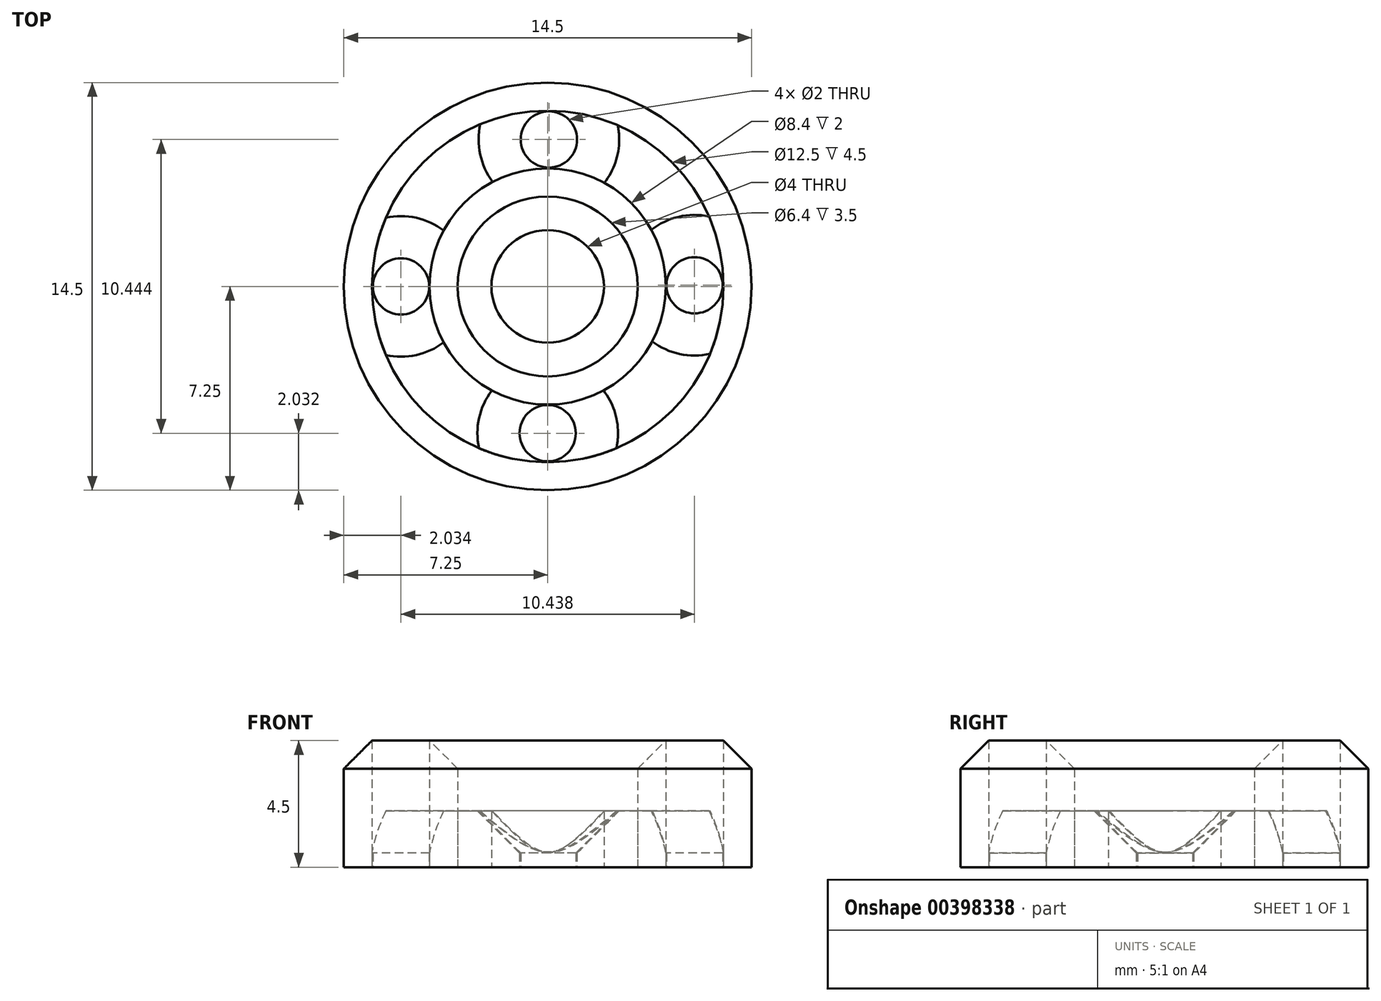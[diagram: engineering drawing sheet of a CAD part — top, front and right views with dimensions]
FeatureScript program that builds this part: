
annotation { "Feature Type Name" : "Feature", "Feature Type Description" : "" }
export const myFeature = defineFeature(function(context is Context, id is Id, definition is map)
    precondition{}
    {
        {
            var Q0;
            Q0=qCreatedBy(makeId("Top.planeOp"),FACE);
            var sketch = newSketch(context, id + "F0", { "sketchPlane" : qUnion([Q0])});
            skCircle(sketch, "E0", {"center": v(0, 0) * mm, "radius": 3.2 * mm});
            skCircle(sketch, "E1", {"center": v(0, 0) * mm, "radius": 4.2 * mm});
            skCircle(sketch, "E2", {"center": v(0, 0) * mm, "radius": 6.25 * mm});
            skCircle(sketch, "E3", {"center": v(0, 0) * mm, "radius": 7.25 * mm});
            skCircle(sketch, "E4", {"center": v(-5.22, 0) * mm, "radius": 1 * mm});
            skCircle(sketch, "E5", {"center": v(0, -5.22) * mm, "radius": 1 * mm});
            skCircle(sketch, "E6", {"center": v(0, 0) * mm, "radius": 2 * mm});
            skCircle(sketch, "E7", {"center": v(5.22, 0.04) * mm, "radius": 1 * mm});
            skCircle(sketch, "E8", {"center": v(0.04, 5.23) * mm, "radius": 1 * mm});
            skSolve(sketch);
        }
        {
            var Q0;
            Q0=makeQuery(id+"F0.imprint","IMPRINT",FACE,{"disambiguationData":[TD([[makeQuery(id+"F0.imprint","IMPRINT",EDGE,{"derivedFrom":sQuery(id+"F0.wireOp",EDGE,"E2")}),-1.0]])]});
            var Q1;
            Q1=makeQuery(id+"F0.imprint","IMPRINT",FACE,{"disambiguationData":[TD([[makeQuery(id+"F0.imprint","IMPRINT",EDGE,{"derivedFrom":sQuery(id+"F0.wireOp",EDGE,"E0")}),-1.0]])]});
            extrude(context, id + "F1", {"entities" : qUnion([Q0, Q1]), "depth" : 5 * mm});
        }
        {
            var Q0;
            Q0=makeQuery(id+"F0.imprint","IMPRINT",FACE,{"disambiguationData":[TD([[makeQuery(id+"F0.imprint","IMPRINT",EDGE,{"derivedFrom":sQuery(id+"F0.wireOp",EDGE,"E0")}),1.0]])]});
            var Q1;
            Q1=makeQuery(id+"F0.imprint","IMPRINT",FACE,{"disambiguationData":[TD([[makeQuery(id+"F0.imprint","IMPRINT",EDGE,{"derivedFrom":sQuery(id+"F0.wireOp",EDGE,"E2")}),1.0]])]});
            extrude(context, id + "F2", {"entities" : qUnion([Q0, Q1]), "depth" : 2 * mm});
        }
        {
            var Q0;
            Q0=makeQuery(id+"F2.opExtrude","CAP_EDGE",EDGE,{"disambiguationData":[OSD([sQuery(id+"F0.wireOp",EDGE,"E4")])],"isStart":false});
            var Q1;
            Q1=makeQuery(id+"F2.opExtrude","CAP_EDGE",EDGE,{"disambiguationData":[OSD([sQuery(id+"F0.wireOp",EDGE,"E5")])],"isStart":false});
            var Q2;
            Q2=makeQuery(id+"F1.opExtrude","CAP_EDGE",EDGE,{"disambiguationData":[OSD([sQuery(id+"F0.wireOp",EDGE,"E0")])],"isStart":false});
            var Q3;
            Q3=makeQuery(id+"F1.opExtrude","CAP_EDGE",EDGE,{"disambiguationData":[OSD([sQuery(id+"F0.wireOp",EDGE,"E3")])],"isStart":false});
            var Q4;
            Q4=makeQuery(id+"F2.opExtrude","CAP_EDGE",EDGE,{"disambiguationData":[OSD([sQuery(id+"F0.wireOp",EDGE,"E8")])],"isStart":false});
            var Q5;
            Q5=makeQuery(id+"F2.opExtrude","CAP_EDGE",EDGE,{"disambiguationData":[OSD([sQuery(id+"F0.wireOp",EDGE,"E7")])],"isStart":false});
            chamfer(context, id + "F3", {"entities" : qUnion([Q0, Q1, Q2, Q3, Q4, Q5]), "width" : 1.5 * mm, "tangentPropagation" : true});
        }
    });
